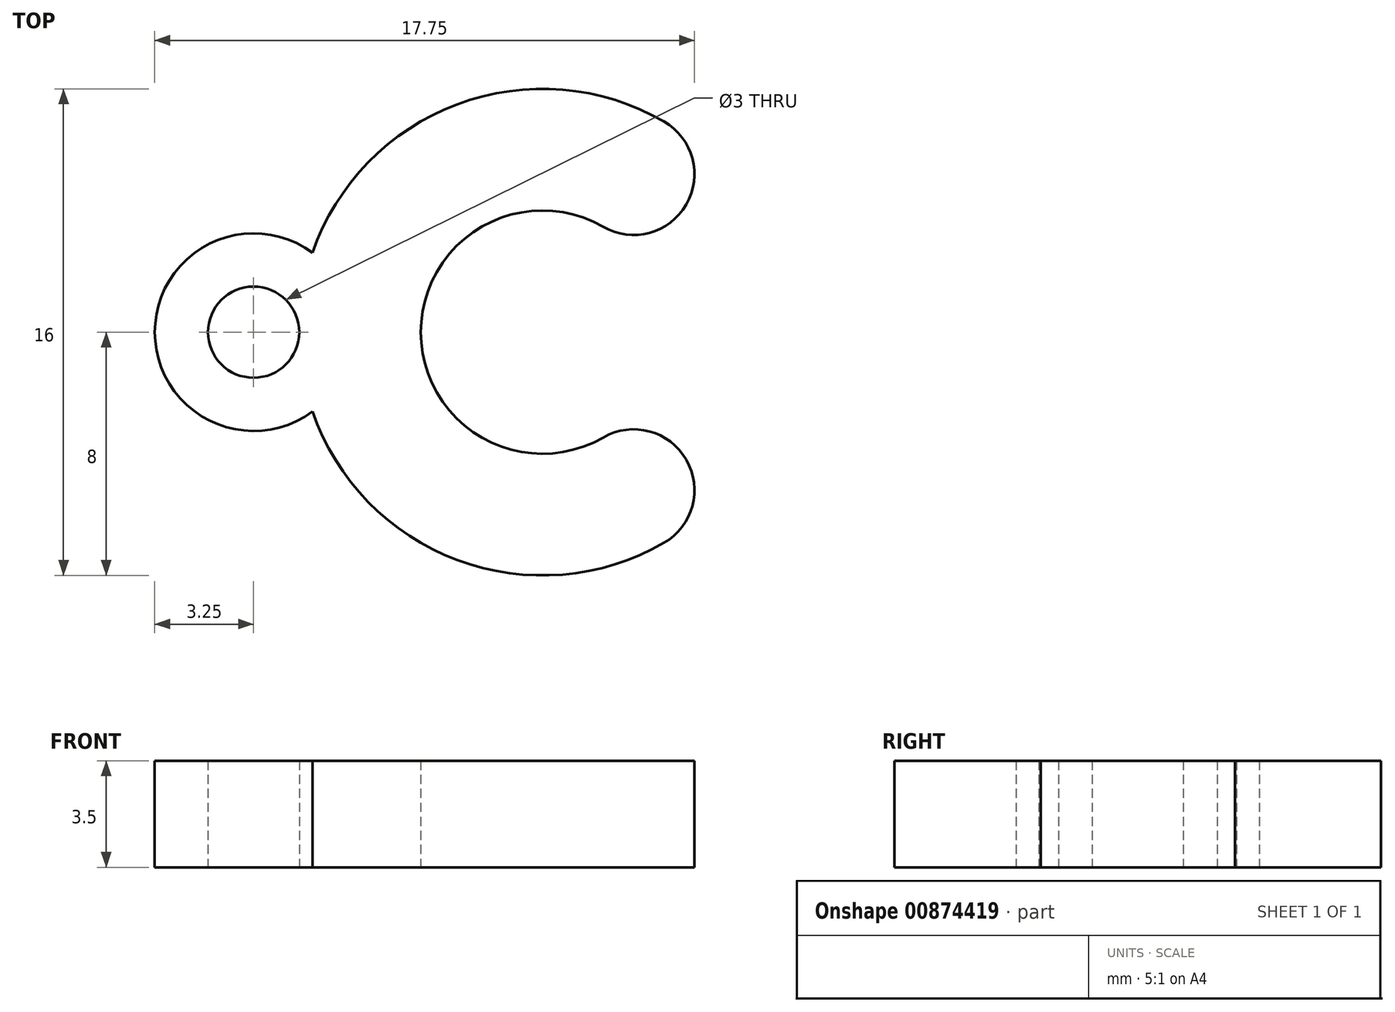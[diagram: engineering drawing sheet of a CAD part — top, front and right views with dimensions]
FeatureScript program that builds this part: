
annotation { "Feature Type Name" : "Feature", "Feature Type Description" : "" }
export const myFeature = defineFeature(function(context is Context, id is Id, definition is map)
    precondition{}
    {
        {
            var Q0;
            Q0=qCreatedBy(makeId("Top.planeOp"),FACE);
            var sketch = newSketch(context, id + "F0", { "sketchPlane" : qUnion([Q0])});
            skPoint(sketch, "E0.middle", {"position": v(0, 0) * mm});
            skCircle(sketch, "E1", {"center": v(-9.5, 0) * mm, "radius": 1.5 * mm});
            skArc(sketch, "E2", {"start": v(-7.56, 2.6) * mm, "mid": v(-12.75, 0) * mm, "end": v(-7.56, -2.6) * mm});
            skArc(sketch, "E3.converted", {"start": v(2, 3.46) * mm, "mid": v(-4, 0) * mm, "end": v(2, -3.46) * mm});
            skArc(sketch, "E4", {"start": v(-7.56, -2.6) * mm, "mid": v(-2.8, -7.5) * mm, "end": v(4, -6.93) * mm});
            skLineSegment(sketch, "E5", {"start": v(0, 0) * mm, "end": v(4, 6.93) * mm, "construction": true});
            skLineSegment(sketch, "E6", {"start": v(0, 0) * mm, "end": v(4, -6.93) * mm, "construction": true});
            skArc(sketch, "E7.trimOffspring", {"start": v(4, 6.93) * mm, "mid": v(-2.8, 7.5) * mm, "end": v(-7.56, 2.6) * mm});
            skArc(sketch, "E8", {"start": v(2, 3.46) * mm, "mid": v(4.73, 4.2) * mm, "end": v(4, 6.93) * mm});
            skPoint(sketch, "E8.third.point", {"position": v(4.68, 4.11) * mm});
            skArc(sketch, "E9", {"start": v(4, -6.93) * mm, "mid": v(4.73, -4.2) * mm, "end": v(2, -3.46) * mm});
            skPoint(sketch, "E9.third.point", {"position": v(4.7, -4.13) * mm});
            skSolve(sketch);
        }
        {
            var Q0;
            Q0=makeQuery(id+"F0.imprint","IMPRINT",FACE,{"disambiguationData":[TD([[makeQuery(id+"F0.imprint","IMPRINT",EDGE,{"derivedFrom":sQuery(id+"F0.wireOp",EDGE,"E1")}),-1.0]])]});
            extrude(context, id + "F1", {"entities" : qUnion([Q0]), "depth" : 3.5 * mm, "offsetDistance" : 25 * mm});
        }
    });
